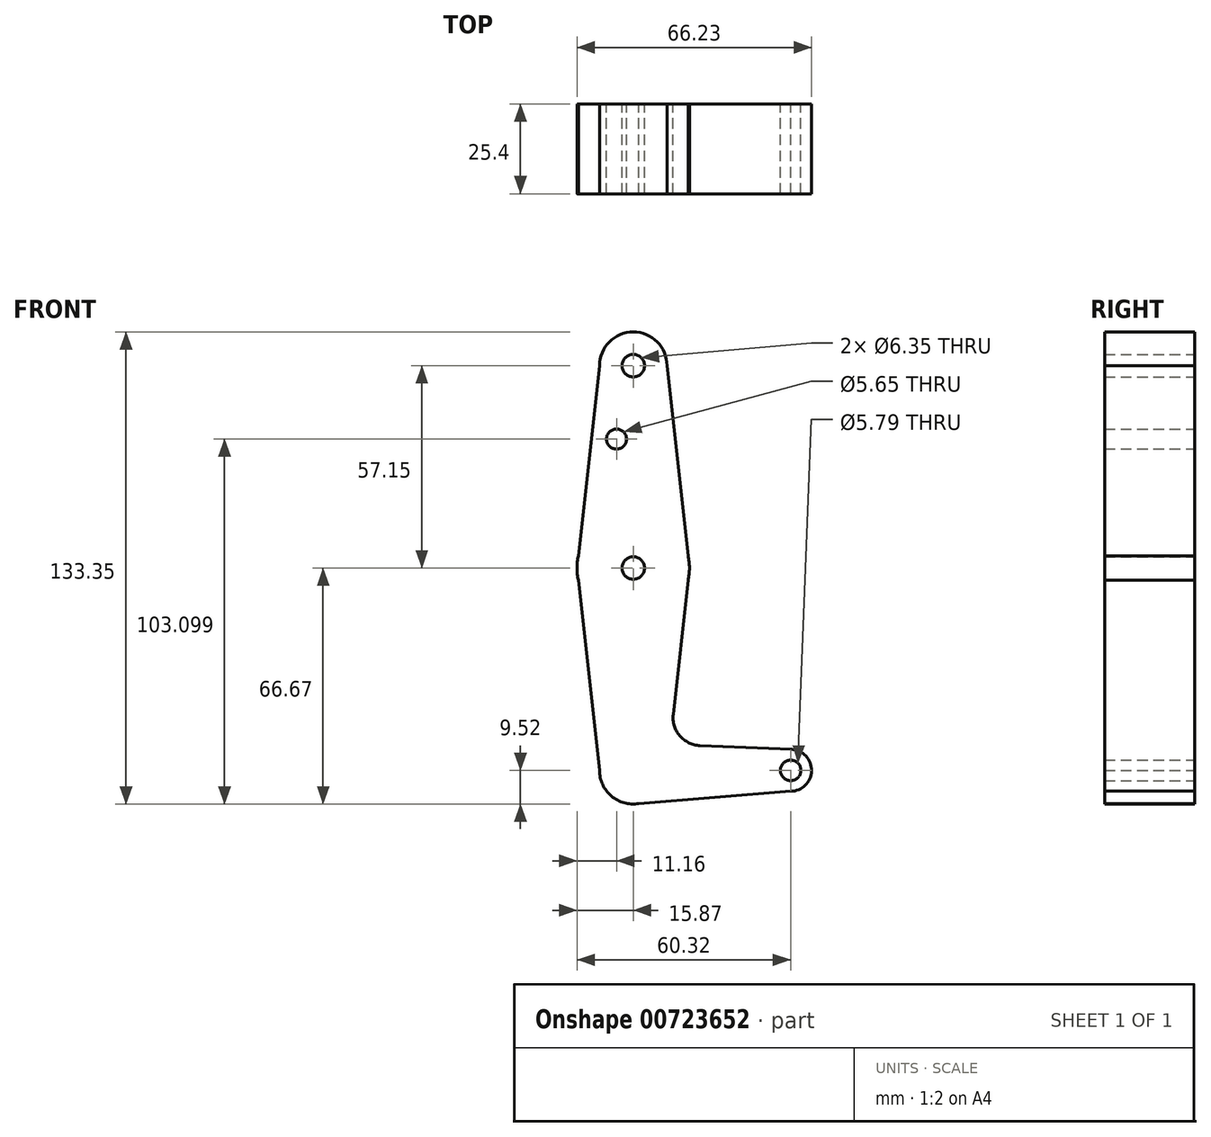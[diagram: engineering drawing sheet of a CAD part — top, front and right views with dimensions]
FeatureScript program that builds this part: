
annotation { "Feature Type Name" : "Feature", "Feature Type Description" : "" }
export const myFeature = defineFeature(function(context is Context, id is Id, definition is map)
    precondition{}
    {
        {
            var Q0;
            Q0=qCreatedBy(makeId("Front.planeOp"),FACE);
            var sketch = newSketch(context, id + "F0", { "sketchPlane" : qUnion([Q0])});
            skLineSegment(sketch, "E0", {"start": v(0, 114.3) * mm, "end": v(0, 0) * mm, "construction": true});
            skCircle(sketch, "E1", {"center": v(0, 114.3) * mm, "radius": 9.53 * mm});
            skCircle(sketch, "E2", {"center": v(0, 57.15) * mm, "radius": 15.88 * mm});
            skCircle(sketch, "E3", {"center": v(0, 0) * mm, "radius": 9.53 * mm});
            skCircle(sketch, "E4", {"center": v(44.45, 0) * mm, "radius": 5.9 * mm});
            skLineSegment(sketch, "E5", {"start": v(-9.53, 114.3) * mm, "end": v(-15.88, 57.15) * mm});
            skLineSegment(sketch, "E6", {"start": v(-15.88, 57.15) * mm, "end": v(-9.52, 0) * mm});
            skLineSegment(sketch, "E7", {"start": v(9.52, 114.3) * mm, "end": v(15.88, 57.15) * mm});
            skLineSegment(sketch, "E8", {"start": v(15.88, 57.15) * mm, "end": v(11.28, 15.83) * mm});
            skLineSegment(sketch, "E9", {"start": v(18.85, 7) * mm, "end": v(44.7, 5.9) * mm});
            skLineSegment(sketch, "E10", {"start": v(0, -9.52) * mm, "end": v(44.45, -5.9) * mm});
            skCircle(sketch, "E11", {"center": v(0, 114.3) * mm, "radius": 3.18 * mm});
            skCircle(sketch, "E12", {"center": v(0, 57.15) * mm, "radius": 3.18 * mm});
            skCircle(sketch, "E13", {"center": v(44.45, 0) * mm, "radius": 2.9 * mm});
            skCircle(sketch, "E14", {"center": v(-4.7, 93.58) * mm, "radius": 2.82 * mm});
            skPoint(sketch, "E15.newPointA", {"position": v(9.52, 0) * mm});
            skArc(sketch, "E15.filletArc", {"start": v(11.28, 15.83) * mm, "mid": v(13.15, 9.78) * mm, "end": v(18.85, 7) * mm});
            skLineSegment(sketch, "E16", {"start": v(0, 0) * mm, "end": v(-9.52, 0) * mm});
            skLineSegment(sketch, "E17", {"start": v(0, 0) * mm, "end": v(0, -9.52) * mm});
            skLineSegment(sketch, "E18", {"start": v(0, 0) * mm, "end": v(44.45, 0) * mm, "construction": true});
            skSolve(sketch);
        }
        {
            var Q0;
            Q0 = qSketchRegion(id + "F0", true);
            extrude(context, id + "F1", {"entities" : qUnion([Q0]), "depth" : 25.4 * mm, "offsetDistance" : 25.4 * mm});
        }
    });
